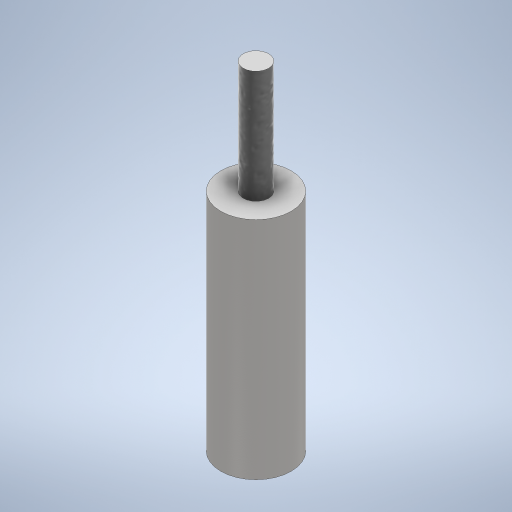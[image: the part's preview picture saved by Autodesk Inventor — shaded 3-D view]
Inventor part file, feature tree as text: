
AUTODESK INVENTOR PART (.ipt)
format: ipt  version: 2024 (Build 280153000, 153)  size: 256,000 bytes
history: native  units: in
note: dims shown in document units (in); Inventor stores cm internally (conversion verified against a paired STEP export)
features: extrude x2, sketch x2
ambient origin geometry x8: Origin, YZ Plane, XZ Plane, XY Plane, X Axis, Y Axis, Z Axis, Center Point
bodies: Solid1 (feature_tree)
feature tree (4):
  extrude  "Extrusion1"  Depth=3.1496in TaperAngle=0.0deg
  extrude  "Extrusion2"  Depth=1.5748in TaperAngle=0.0deg
  sketch  "Sketch1"  dims[d0=0.9843in d1=3.1496in d2=0.0in]
  sketch  "Sketch2"  dims[d3=0.3543in d4=1.5748in d5=0.0in]
